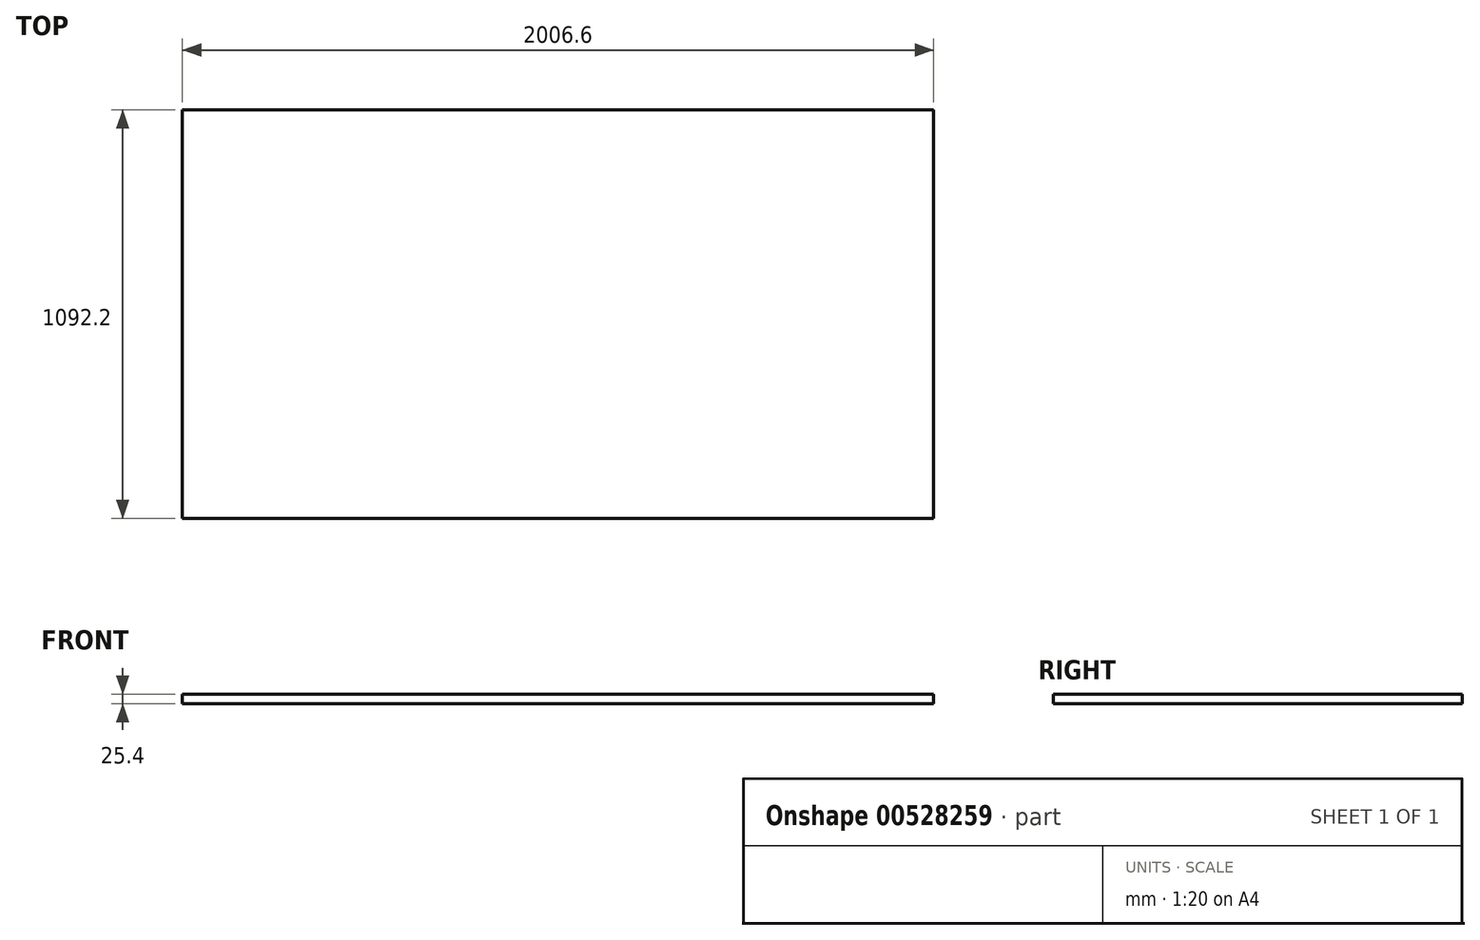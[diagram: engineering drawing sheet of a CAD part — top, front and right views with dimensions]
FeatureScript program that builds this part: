
annotation { "Feature Type Name" : "Feature", "Feature Type Description" : "" }
export const myFeature = defineFeature(function(context is Context, id is Id, definition is map)
    precondition{}
    {
        {
            var Q0;
            Q0=qCreatedBy(makeId("Top.planeOp"),FACE);
            var sketch = newSketch(context, id + "F0", { "sketchPlane" : qUnion([Q0])});
            skLineSegment(sketch, "E0.bottom", {"start": v(1003.3, 546.1) * mm, "end": v(-1003.3, 546.1) * mm});
            skLineSegment(sketch, "E0.top", {"start": v(1003.3, -546.1) * mm, "end": v(-1003.3, -546.1) * mm});
            skLineSegment(sketch, "E0.left", {"start": v(1003.3, 546.1) * mm, "end": v(1003.3, -546.1) * mm});
            skLineSegment(sketch, "E0.right", {"start": v(-1003.3, 546.1) * mm, "end": v(-1003.3, -546.1) * mm});
            skPoint(sketch, "E0.middle", {"position": v(0, 0) * mm});
            skSolve(sketch);
        }
        {
            var Q0;
            Q0 = qSketchRegion(id + "F0", true);
            extrude(context, id + "F1", {"entities" : qUnion([Q0]), "depth" : 25.4 * mm, "offsetDistance" : 25.4 * mm});
        }
    });
